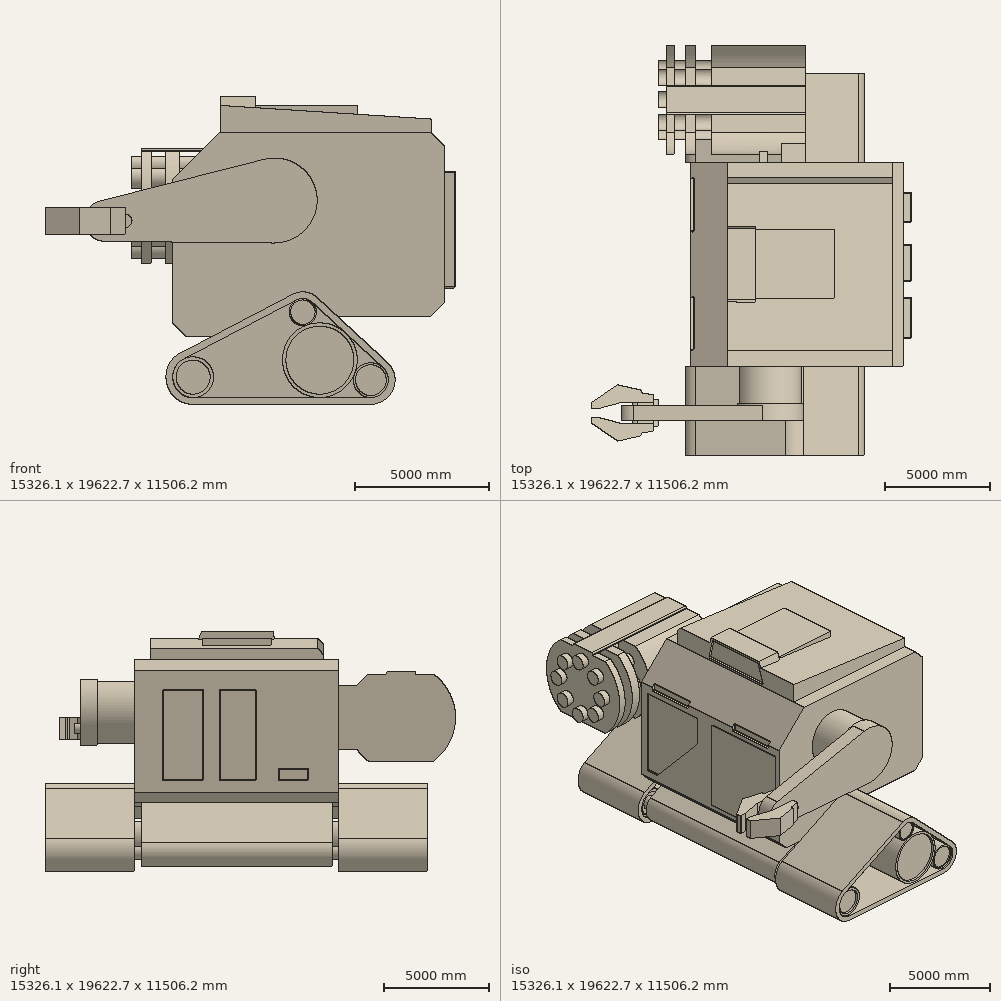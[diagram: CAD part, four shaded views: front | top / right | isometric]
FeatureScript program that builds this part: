
annotation { "Feature Type Name" : "Feature", "Feature Type Description" : "" }
export const myFeature = defineFeature(function(context is Context, id is Id, definition is map)
    precondition{}
    {
        {
            var Q0;
            Q0=qCreatedBy(makeId("Front.planeOp"),FACE);
            var sketch = newSketch(context, id + "F0", { "sketchPlane" : qUnion([Q0])});
            skCircle(sketch, "E0", {"center": v(762, 762) * mm, "radius": 762 * mm});
            skSolve(sketch);
        }
        {
            var Q0;
            Q0 = qSketchRegion(id + "F0", true);
            extrude(context, id + "F1", {"entities" : qUnion([Q0]), "oppositeDirection" : true, "depth" : 4064 * mm});
        }
        {
            var Q0;
            Q0=makeQuery(id+"F1.opExtrude","CAP_FACE",FACE,{"disambiguationData":[OSD([sQuery(id+"F0.wireOp",EDGE,"E0")])],"isStart":true});
            var sketch = newSketch(context, id + "F2", { "sketchPlane" : qUnion([Q0])});
            skCircle(sketch, "E1", {"center": v(762, 762) * mm, "radius": 635 * mm});
            skSolve(sketch);
        }
        {
            var Q0;
            Q0 = qSketchRegion(id + "F2", true);
            extrude(context, id + "F3", {"entities" : qUnion([Q0]), "operationType" : NewBodyOperationType.REMOVE, "oppositeDirection" : true, "depth" : 127 * mm});
        }
        {
            var Q0;
            Q0=makeQuery(id+"F1.opExtrude","CAP_FACE",FACE,{"disambiguationData":[OSD([sQuery(id+"F0.wireOp",EDGE,"E0")])],"isStart":false});
            var sketch = newSketch(context, id + "F4", { "sketchPlane" : qUnion([Q0])});
            skCircle(sketch, "E2", {"center": v(-762, 762) * mm, "radius": 635 * mm});
            skSolve(sketch);
        }
        {
            var Q0;
            Q0 = qSketchRegion(id + "F4", true);
            extrude(context, id + "F5", {"entities" : qUnion([Q0]), "operationType" : NewBodyOperationType.REMOVE, "oppositeDirection" : true, "depth" : 127 * mm});
        }
        {
            var Q0;
            Q0=qCreatedBy(makeId("Front.planeOp"),FACE);
            var sketch = newSketch(context, id + "F6", { "sketchPlane" : qUnion([Q0])});
            skLineSegment(sketch, "E3", {"start": v(0, 0) * mm, "end": v(8804.61, 0) * mm});
            skCircle(sketch, "E4", {"center": v(5497.48, 1397) * mm, "radius": 1397 * mm});
            skPoint(sketch, "E5", {"position": v(417.48, 431.63) * mm});
            skSolve(sketch);
        }
        {
            var Q0;
            Q0 = qSketchRegion(id + "F6", true);
            extrude(context, id + "F7", {"entities" : qUnion([Q0]), "oppositeDirection" : true, "depth" : 4064 * mm});
        }
        {
            var Q0;
            Q0=makeQuery(id+"F7.opExtrude","CAP_FACE",FACE,{"disambiguationData":[OSD([sQuery(id+"F6.wireOp",EDGE,"E4")])],"isStart":true});
            var sketch = newSketch(context, id + "F8", { "sketchPlane" : qUnion([Q0])});
            skCircle(sketch, "E6", {"center": v(5497.48, 1397) * mm, "radius": 1270 * mm});
            skSolve(sketch);
        }
        {
            var Q0;
            Q0 = qSketchRegion(id + "F8", true);
            extrude(context, id + "F9", {"entities" : qUnion([Q0]), "operationType" : NewBodyOperationType.REMOVE, "oppositeDirection" : true, "depth" : 127 * mm});
        }
        {
            var Q0;
            Q0=makeQuery(id+"F7.opExtrude","CAP_FACE",FACE,{"disambiguationData":[OSD([sQuery(id+"F6.wireOp",EDGE,"E4")])],"isStart":false});
            var sketch = newSketch(context, id + "F10", { "sketchPlane" : qUnion([Q0])});
            skCircle(sketch, "E7", {"center": v(-5497.48, 1397) * mm, "radius": 1270 * mm});
            skSolve(sketch);
        }
        {
            var Q0;
            Q0 = qSketchRegion(id + "F10", true);
            extrude(context, id + "F11", {"entities" : qUnion([Q0]), "operationType" : NewBodyOperationType.REMOVE, "oppositeDirection" : true, "depth" : 127 * mm});
        }
        {
            var Q0;
            Q0=qCreatedBy(makeId("Front.planeOp"),FACE);
            var sketch = newSketch(context, id + "F12", { "sketchPlane" : qUnion([Q0])});
            skCircle(sketch, "E8", {"center": v(4862.48, 3193.05) * mm, "radius": 508 * mm});
            skPoint(sketch, "E9", {"position": v(5497.48, 1397) * mm});
            skSolve(sketch);
        }
        {
            var Q0;
            Q0 = qSketchRegion(id + "F12", true);
            extrude(context, id + "F13", {"entities" : qUnion([Q0]), "operationType" : NewBodyOperationType.ADD, "oppositeDirection" : true, "depth" : 4064 * mm});
        }
        {
            var Q0;
            Q0=makeQuery(id+"F13.opExtrude","CAP_FACE",FACE,{"disambiguationData":[OSD([sQuery(id+"F12.wireOp",EDGE,"E8")])],"isStart":true});
            var sketch = newSketch(context, id + "F14", { "sketchPlane" : qUnion([Q0])});
            skCircle(sketch, "E10", {"center": v(4862.48, 3193.05) * mm, "radius": 457.2 * mm});
            skSolve(sketch);
        }
        {
            var Q0;
            Q0 = qSketchRegion(id + "F14", true);
            extrude(context, id + "F15", {"entities" : qUnion([Q0]), "operationType" : NewBodyOperationType.REMOVE, "oppositeDirection" : true, "depth" : 50.8 * mm});
        }
        {
            var Q0;
            Q0=makeQuery(id+"F13.opExtrude","CAP_FACE",FACE,{"disambiguationData":[OSD([sQuery(id+"F12.wireOp",EDGE,"E8")])],"isStart":false});
            var sketch = newSketch(context, id + "F16", { "sketchPlane" : qUnion([Q0])});
            skCircle(sketch, "E11", {"center": v(-4862.48, 3193.05) * mm, "radius": 457.2 * mm});
            skSolve(sketch);
        }
        {
            var Q0;
            Q0 = qSketchRegion(id + "F16", true);
            extrude(context, id + "F17", {"entities" : qUnion([Q0]), "operationType" : NewBodyOperationType.REMOVE, "oppositeDirection" : true, "depth" : 50.8 * mm});
        }
        {
            var Q0;
            Q0=qCreatedBy(makeId("Front.planeOp"),FACE);
            var sketch = newSketch(context, id + "F18", { "sketchPlane" : qUnion([Q0])});
            skLineSegment(sketch, "E12", {"start": v(330.5, 1396.25) * mm, "end": v(4640.98, 3650.5) * mm});
            skLineSegment(sketch, "E13", {"start": v(5195.5, 3576.98) * mm, "end": v(7846.69, 1129.63) * mm});
            skLineSegment(sketch, "E14", {"start": v(7405, 0) * mm, "end": v(673.56, 0) * mm});
            skArc(sketch, "E15", {"start": v(673.56, 0) * mm, "mid": v(17.04, 578.96) * mm, "end": v(330.5, 1396.25) * mm});
            skPoint(sketch, "E16.orphan", {"position": v(-2339.36, 0) * mm});
            skArc(sketch, "E17", {"start": v(4640.98, 3650.5) * mm, "mid": v(4929.27, 3696.89) * mm, "end": v(5195.5, 3576.98) * mm});
            skArc(sketch, "E18", {"start": v(7405, 0) * mm, "mid": v(8011.46, 414.04) * mm, "end": v(7846.69, 1129.63) * mm});
            skPoint(sketch, "E19.orphan", {"position": v(9070.4, 0) * mm});
            skLineSegment(sketch, "E20", {"start": v(212.8, 1621.33) * mm, "end": v(4520.5, 3874.12) * mm});
            skLineSegment(sketch, "E21", {"start": v(673.56, -254) * mm, "end": v(7405, -254) * mm});
            skLineSegment(sketch, "E22", {"start": v(5381.15, 3751.28) * mm, "end": v(8018.98, 1316.26) * mm});
            skArc(sketch, "E23", {"start": v(673.56, -254) * mm, "mid": v(-228.39, 518.66) * mm, "end": v(212.8, 1621.33) * mm});
            skArc(sketch, "E24", {"start": v(4520.5, 3874.12) * mm, "mid": v(4975.09, 3946.79) * mm, "end": v(5388.58, 3744.42) * mm});
            skArc(sketch, "E25", {"start": v(7405, -254) * mm, "mid": v(8248.02, 321.55) * mm, "end": v(8018.98, 1316.26) * mm});
            skSolve(sketch);
        }
        {
            var Q0;
            Q0 = qSketchRegion(id + "F18", true);
            extrude(context, id + "F19", {"entities" : qUnion([Q0]), "oppositeDirection" : true, "depth" : 4165.6 * mm, "hasSecondDirection" : true, "secondDirectionOppositeDirection" : false, "secondDirectionDepth" : 101.6 * mm});
        }
        {
            var Q0;
            Q0=qCreatedBy(makeId("Front.planeOp"),FACE);
            var sketch = newSketch(context, id + "F20", { "sketchPlane" : qUnion([Q0])});
            skCircle(sketch, "E26", {"center": v(7405, 651.16) * mm, "radius": 651.16 * mm});
            skSolve(sketch);
        }
        {
            var Q0;
            Q0 = qSketchRegion(id + "F20", true);
            extrude(context, id + "F21", {"entities" : qUnion([Q0]), "oppositeDirection" : true, "depth" : 4064 * mm});
        }
        {
            var Q0;
            Q0=makeQuery(id+"F21.opExtrude","CAP_FACE",FACE,{"disambiguationData":[OSD([sQuery(id+"F20.wireOp",EDGE,"E26")])],"isStart":false});
            var sketch = newSketch(context, id + "F22", { "sketchPlane" : qUnion([Q0])});
            skCircle(sketch, "E27", {"center": v(-7405, 651.16) * mm, "radius": 574.96 * mm});
            skSolve(sketch);
        }
        {
            var Q0;
            Q0 = qSketchRegion(id + "F22", true);
            extrude(context, id + "F23", {"entities" : qUnion([Q0]), "operationType" : NewBodyOperationType.REMOVE, "oppositeDirection" : true, "depth" : 76.2 * mm});
        }
        {
            var Q0;
            Q0=makeQuery(id+"F21.opExtrude","CAP_FACE",FACE,{"disambiguationData":[OSD([sQuery(id+"F20.wireOp",EDGE,"E26")])],"isStart":true});
            var sketch = newSketch(context, id + "F24", { "sketchPlane" : qUnion([Q0])});
            skCircle(sketch, "E28", {"center": v(7405, 651.16) * mm, "radius": 574.96 * mm});
            skSolve(sketch);
        }
        {
            var Q0;
            Q0 = qSketchRegion(id + "F24", true);
            extrude(context, id + "F25", {"entities" : qUnion([Q0]), "operationType" : NewBodyOperationType.REMOVE, "oppositeDirection" : true, "depth" : 76.2 * mm});
        }
        {
            var Q0;
            Q0=makeQuery(id+"F11.boolean.opBoolean","COPY",FACE,{"derivedFrom":makeQuery(id+"F11.opExtrude","CAP_FACE",FACE,{"disambiguationData":[OSD([sQuery(id+"F10.wireOp",EDGE,"E7")])],"isStart":false})});
            var sketch = newSketch(context, id + "F26", { "sketchPlane" : qUnion([Q0])});
            skCircle(sketch, "E29", {"center": v(-5497.48, 1397) * mm, "radius": 762 * mm});
            skCircle(sketch, "E30", {"center": v(-762, 762) * mm, "radius": 381 * mm});
            skCircle(sketch, "E31", {"center": v(-7405, 651.16) * mm, "radius": 320.96 * mm});
            skCircle(sketch, "E32", {"center": v(-4862.48, 3193.05) * mm, "radius": 330.2 * mm});
            skSolve(sketch);
        }
        {
            var Q0;
            Q0 = qSketchRegion(id + "F26", true);
            extrude(context, id + "F27", {"entities" : qUnion([Q0]), "depth" : 5080 * mm, "hasSecondDirection" : true, "secondDirectionOppositeDirection" : true, "secondDirectionDepth" : 254 * mm});
        }
        {
            var Q0;
            Q0=makeQuery(id+"F27.opExtrude","CAP_FACE",FACE,{"disambiguationData":[OSD([sQuery(id+"F26.wireOp",EDGE,"E32")])],"isStart":false});
            cPlane(context, id + "F28", {"entities" : qUnion([Q0]), "cplaneType" : CPlaneType.OFFSET, "offset" : 25.4 * mm, "width" : 152.4 * mm, "height" : 152.4 * mm});
        }
        {
            var Q0;
            Q0=makeQuery(id+"F1.opExtrude","SWEPT_BODY",BODY,{"disambiguationData":[OSD([sQuery(id+"F0.wireOp",EDGE,"E0")])]});
            var Q1;
            Q1=makeQuery(id+"F7.opExtrude","SWEPT_BODY",BODY,{"disambiguationData":[OSD([sQuery(id+"F6.wireOp",EDGE,"E4")])]});
            var Q2;
            Q2=makeQuery(id+"F13.opExtrude","SWEPT_BODY",BODY,{"disambiguationData":[OSD([sQuery(id+"F12.wireOp",EDGE,"E8")])]});
            var Q3;
            Q3=makeQuery(id+"F27.opExtrude","SWEPT_BODY",BODY,{"disambiguationData":[OSD([sQuery(id+"F26.wireOp",EDGE,"E32")])]});
            var Q4;
            Q4=makeQuery(id+"F27.opExtrude","SWEPT_BODY",BODY,{"disambiguationData":[OSD([sQuery(id+"F26.wireOp",EDGE,"E31")])]});
            var Q5;
            Q5=makeQuery(id+"F27.opExtrude","SWEPT_BODY",BODY,{"disambiguationData":[OSD([sQuery(id+"F26.wireOp",EDGE,"E30")])]});
            var Q6;
            Q6=makeQuery(id+"F27.opExtrude","SWEPT_BODY",BODY,{"disambiguationData":[OSD([sQuery(id+"F26.wireOp",EDGE,"E29")])]});
            var Q7;
            Q7=makeQuery(id+"F21.opExtrude","SWEPT_BODY",BODY,{"disambiguationData":[OSD([sQuery(id+"F20.wireOp",EDGE,"E26")])]});
            var Q8;
            Q8=makeQuery(id+"F19.opExtrude","SWEPT_BODY",BODY,{"disambiguationData":[OSD([sQuery(id+"F18.wireOp",EDGE,"E12"),sQuery(id+"F18.wireOp",EDGE,"E13"),sQuery(id+"F18.wireOp",EDGE,"E14"),sQuery(id+"F18.wireOp",EDGE,"E15"),sQuery(id+"F18.wireOp",EDGE,"E17"),sQuery(id+"F18.wireOp",EDGE,"E18"),sQuery(id+"F18.wireOp",EDGE,"E20"),sQuery(id+"F18.wireOp",EDGE,"E21"),sQuery(id+"F18.wireOp",EDGE,"E22"),sQuery(id+"F18.wireOp",EDGE,"E23"),sQuery(id+"F18.wireOp",EDGE,"E24"),sQuery(id+"F18.wireOp",EDGE,"E25")])]});
            var Q9;
            Q9=qCreatedBy(id+"F28.planeOp",FACE);
            mirror(context, id + "F29", {"entities" : qUnion([Q0, Q1, Q2, Q3, Q4, Q5, Q6, Q7, Q8]), "mirrorPlane" : qUnion([Q9])});
        }
        {
            var Q0;
            Q0=qCreatedBy(id+"F28.planeOp",FACE);
            var sketch = newSketch(context, id + "F30", { "sketchPlane" : qUnion([Q0])});
            skLineSegment(sketch, "E33", {"start": v(-4640.98, 3650.5) * mm, "end": v(-330.5, 1396.25) * mm});
            skLineSegment(sketch, "E34", {"start": v(-7846.69, 1129.63) * mm, "end": v(-5195.5, 3576.98) * mm});
            skLineSegment(sketch, "E35", {"start": v(-673.56, 0) * mm, "end": v(-7405, 0) * mm});
            skPoint(sketch, "E36", {"position": v(-4862.48, 3193.05) * mm});
            skArc(sketch, "E37", {"start": v(-5195.5, 3576.98) * mm, "mid": v(-4929.27, 3696.89) * mm, "end": v(-4640.98, 3650.5) * mm});
            skPoint(sketch, "E38", {"position": v(-762, 762) * mm});
            skArc(sketch, "E39", {"start": v(-330.5, 1396.25) * mm, "mid": v(-17.04, 578.96) * mm, "end": v(-673.56, 0) * mm});
            skPoint(sketch, "E40", {"position": v(-7405, 651.16) * mm});
            skArc(sketch, "E41", {"start": v(-7405, 0) * mm, "mid": v(-8011.46, 414.04) * mm, "end": v(-7846.69, 1129.63) * mm});
            skSolve(sketch);
        }
        {
            var Q0;
            Q0 = qSketchRegion(id + "F30", true);
            extrude(context, id + "F31", {"entities" : qUnion([Q0]), "depth" : 4572 * mm, "hasSecondDirection" : true, "secondDirectionOppositeDirection" : true, "secondDirectionDepth" : 4572 * mm});
        }
        {
            var Q0;
            Q0=qCreatedBy(id+"F28.planeOp",FACE);
            var sketch = newSketch(context, id + "F32", { "sketchPlane" : qUnion([Q0])});
            skLineSegment(sketch, "E42", {"start": v(-5768.54, 3048) * mm, "end": v(-10160, 3048) * mm});
            skLineSegment(sketch, "E43", {"start": v(-10160, 3048) * mm, "end": v(-10160, 9906) * mm});
            skLineSegment(sketch, "E44", {"start": v(-10160, 9906) * mm, "end": v(0, 9906) * mm});
            skLineSegment(sketch, "E45", {"start": v(0, 9906) * mm, "end": v(0, 2286) * mm});
            skLineSegment(sketch, "E46", {"start": v(0, 2286) * mm, "end": v(-2031.85, 2286) * mm});
            skPoint(sketch, "E47", {"position": v(-4862.48, 3193.05) * mm});
            skPoint(sketch, "E48.orphan", {"position": v(-4984.96, 4117.02) * mm});
            skArc(sketch, "E49", {"start": v(-5226.07, 3547.92) * mm, "mid": v(-4934.21, 3696.03) * mm, "end": v(-4612.58, 3635.42) * mm});
            skLineSegment(sketch, "E50", {"start": v(-5768.54, 3048) * mm, "end": v(-5226.07, 3547.92) * mm});
            skLineSegment(sketch, "E51", {"start": v(-4612.58, 3635.42) * mm, "end": v(-2031.85, 2286) * mm});
            skSolve(sketch);
        }
        {
            var Q0;
            Q0 = qSketchRegion(id + "F32", true);
            extrude(context, id + "F33", {"entities" : qUnion([Q0]), "depth" : 4876.8 * mm, "hasSecondDirection" : true, "secondDirectionOppositeDirection" : true, "secondDirectionDepth" : 4876.8 * mm});
        }
        {
            var Q0;
            Q0=makeQuery(id+"F33.opExtrude","SWEPT_EDGE",EDGE,{"disambiguationData":[OSD([sQuery(id+"F32.wireOp",EDGE,"E44"),sQuery(id+"F32.wireOp",EDGE,"E45")])]});
            chamfer(context, id + "F34", {"entities" : qUnion([Q0]), "width" : 1778 * mm, "tangentPropagation" : true});
        }
        {
            var Q0;
            Q0=makeQuery(id+"F33.opExtrude","SWEPT_EDGE",EDGE,{"disambiguationData":[OSD([sQuery(id+"F32.wireOp",EDGE,"E43"),sQuery(id+"F32.wireOp",EDGE,"E44")])]});
            var Q1;
            Q1=makeQuery(id+"F33.opExtrude","SWEPT_EDGE",EDGE,{"disambiguationData":[OSD([sQuery(id+"F32.wireOp",EDGE,"E42"),sQuery(id+"F32.wireOp",EDGE,"E43")])]});
            chamfer(context, id + "F35", {"entities" : qUnion([Q0, Q1]), "width" : 508 * mm, "tangentPropagation" : true});
        }
        {
            var Q0;
            Q0=makeQuery(id+"F33.opExtrude","SWEPT_EDGE",EDGE,{"disambiguationData":[OSD([sQuery(id+"F32.wireOp",EDGE,"E45"),sQuery(id+"F32.wireOp",EDGE,"E46")])]});
            chamfer(context, id + "F36", {"entities" : qUnion([Q0]), "width" : 508 * mm, "tangentPropagation" : true});
        }
        {
            var Q0;
            Q0=makeQuery(id+"F33.opExtrude","SWEPT_FACE",FACE,{"disambiguationData":[OSD([sQuery(id+"F32.wireOp",EDGE,"E43")])]});
            var sketch = newSketch(context, id + "F37", { "sketchPlane" : qUnion([Q0])});
            skLineSegment(sketch, "E52.bottom", {"start": v(5510.46, 8459.44) * mm, "end": v(7459.12, 8459.44) * mm});
            skLineSegment(sketch, "E52.top", {"start": v(5510.46, 4095.25) * mm, "end": v(7459.12, 4095.25) * mm});
            skLineSegment(sketch, "E52.left", {"start": v(5510.46, 8459.44) * mm, "end": v(5510.46, 4095.25) * mm});
            skLineSegment(sketch, "E52.right", {"start": v(7459.12, 8459.44) * mm, "end": v(7459.12, 4095.25) * mm});
            skLineSegment(sketch, "E53.bottom", {"start": v(8230.46, 8459.44) * mm, "end": v(9976.13, 8459.44) * mm});
            skLineSegment(sketch, "E53.top", {"start": v(8230.46, 4095.25) * mm, "end": v(9976.13, 4095.25) * mm});
            skLineSegment(sketch, "E53.left", {"start": v(8230.46, 8459.44) * mm, "end": v(8230.46, 4095.25) * mm});
            skLineSegment(sketch, "E53.right", {"start": v(9976.13, 8459.44) * mm, "end": v(9976.13, 4095.25) * mm});
            skLineSegment(sketch, "E54.bottom", {"start": v(11051.95, 4095.25) * mm, "end": v(12472.85, 4095.25) * mm});
            skLineSegment(sketch, "E54.top", {"start": v(11051.95, 4683.91) * mm, "end": v(12472.85, 4683.91) * mm});
            skLineSegment(sketch, "E54.left", {"start": v(11051.95, 4095.25) * mm, "end": v(11051.95, 4683.91) * mm});
            skLineSegment(sketch, "E54.right", {"start": v(12472.85, 4095.25) * mm, "end": v(12472.85, 4683.91) * mm});
            skSolve(sketch);
        }
        {
            var Q0;
            Q0 = qSketchRegion(id + "F37", true);
            extrude(context, id + "F38", {"entities" : qUnion([Q0]), "operationType" : NewBodyOperationType.ADD, "depth" : 406.4 * mm});
        }
        {
            var Q0;
            Q0=makeQuery(id+"F38.opExtrude","CAP_FACE",FACE,{"disambiguationData":[OSD([sQuery(id+"F37.wireOp",EDGE,"E52.bottom"),sQuery(id+"F37.wireOp",EDGE,"E52.top"),sQuery(id+"F37.wireOp",EDGE,"E52.left"),sQuery(id+"F37.wireOp",EDGE,"E52.right")])],"isStart":false});
            var Q1;
            Q1=makeQuery(id+"F38.opExtrude","CAP_FACE",FACE,{"disambiguationData":[OSD([sQuery(id+"F37.wireOp",EDGE,"E53.bottom"),sQuery(id+"F37.wireOp",EDGE,"E53.top"),sQuery(id+"F37.wireOp",EDGE,"E53.left"),sQuery(id+"F37.wireOp",EDGE,"E53.right")])],"isStart":false});
            var Q2;
            Q2=makeQuery(id+"F38.opExtrude","CAP_FACE",FACE,{"disambiguationData":[OSD([sQuery(id+"F37.wireOp",EDGE,"E54.bottom"),sQuery(id+"F37.wireOp",EDGE,"E54.top"),sQuery(id+"F37.wireOp",EDGE,"E54.left"),sQuery(id+"F37.wireOp",EDGE,"E54.right")])],"isStart":false});
            var Q3;
            Q3=makeQuery(id+"F38.opExtrude","SWEPT_EDGE",EDGE,{"disambiguationData":[OSD([sQuery(id+"F37.wireOp",EDGE,"E52.bottom"),sQuery(id+"F37.wireOp",EDGE,"E52.left")])]});
            var Q4;
            Q4=makeQuery(id+"F38.opExtrude","SWEPT_EDGE",EDGE,{"disambiguationData":[OSD([sQuery(id+"F37.wireOp",EDGE,"E52.bottom"),sQuery(id+"F37.wireOp",EDGE,"E52.right")])]});
            var Q5;
            Q5=makeQuery(id+"F38.opExtrude","SWEPT_EDGE",EDGE,{"disambiguationData":[OSD([sQuery(id+"F37.wireOp",EDGE,"E52.top"),sQuery(id+"F37.wireOp",EDGE,"E52.left")])]});
            var Q6;
            Q6=makeQuery(id+"F38.opExtrude","SWEPT_EDGE",EDGE,{"disambiguationData":[OSD([sQuery(id+"F37.wireOp",EDGE,"E52.top"),sQuery(id+"F37.wireOp",EDGE,"E52.right")])]});
            var Q7;
            Q7=makeQuery(id+"F38.opExtrude","SWEPT_EDGE",EDGE,{"disambiguationData":[OSD([sQuery(id+"F37.wireOp",EDGE,"E53.top"),sQuery(id+"F37.wireOp",EDGE,"E53.left")])]});
            var Q8;
            Q8=makeQuery(id+"F38.opExtrude","SWEPT_EDGE",EDGE,{"disambiguationData":[OSD([sQuery(id+"F37.wireOp",EDGE,"E53.top"),sQuery(id+"F37.wireOp",EDGE,"E53.right")])]});
            var Q9;
            Q9=makeQuery(id+"F38.opExtrude","SWEPT_EDGE",EDGE,{"disambiguationData":[OSD([sQuery(id+"F37.wireOp",EDGE,"E53.bottom"),sQuery(id+"F37.wireOp",EDGE,"E53.right")])]});
            var Q10;
            Q10=makeQuery(id+"F38.opExtrude","SWEPT_EDGE",EDGE,{"disambiguationData":[OSD([sQuery(id+"F37.wireOp",EDGE,"E53.bottom"),sQuery(id+"F37.wireOp",EDGE,"E53.left")])]});
            var Q11;
            Q11=makeQuery(id+"F38.opExtrude","SWEPT_EDGE",EDGE,{"disambiguationData":[OSD([sQuery(id+"F37.wireOp",EDGE,"E54.top"),sQuery(id+"F37.wireOp",EDGE,"E54.left")])]});
            var Q12;
            Q12=makeQuery(id+"F38.opExtrude","SWEPT_EDGE",EDGE,{"disambiguationData":[OSD([sQuery(id+"F37.wireOp",EDGE,"E54.bottom"),sQuery(id+"F37.wireOp",EDGE,"E54.left")])]});
            var Q13;
            Q13=makeQuery(id+"F38.opExtrude","SWEPT_EDGE",EDGE,{"disambiguationData":[OSD([sQuery(id+"F37.wireOp",EDGE,"E54.bottom"),sQuery(id+"F37.wireOp",EDGE,"E54.right")])]});
            var Q14;
            Q14=makeQuery(id+"F38.opExtrude","SWEPT_EDGE",EDGE,{"disambiguationData":[OSD([sQuery(id+"F37.wireOp",EDGE,"E54.top"),sQuery(id+"F37.wireOp",EDGE,"E54.right")])]});
            fillet(context, id + "F39", {"entities" : qUnion([Q0, Q1, Q2, Q3, Q4, Q5, Q6, Q7, Q8, Q9, Q10, Q11, Q12, Q13, Q14]), "radius" : 50.8 * mm, "tangentPropagation" : true, "allowEdgeOverflow" : false});
        }
        {
            var Q0;
            Q0=makeQuery(id+"F33.opExtrude","SWEPT_FACE",FACE,{"disambiguationData":[OSD([sQuery(id+"F32.wireOp",EDGE,"E45")])]});
            var sketch = newSketch(context, id + "F40", { "sketchPlane" : qUnion([Q0])});
            skLineSegment(sketch, "E55.bottom", {"start": v(-13157.2, 8331.2) * mm, "end": v(-10617.2, 8331.2) * mm});
            skLineSegment(sketch, "E55.top", {"start": v(-13157.2, 7924.8) * mm, "end": v(-10617.2, 7924.8) * mm});
            skLineSegment(sketch, "E55.left", {"start": v(-13157.2, 8331.2) * mm, "end": v(-13157.2, 7924.8) * mm});
            skLineSegment(sketch, "E55.right", {"start": v(-10617.2, 8331.2) * mm, "end": v(-10617.2, 7924.8) * mm});
            skLineSegment(sketch, "E56.bottom", {"start": v(-7467.6, 8331.2) * mm, "end": v(-4927.6, 8331.2) * mm});
            skLineSegment(sketch, "E56.top", {"start": v(-7467.6, 7924.8) * mm, "end": v(-4927.6, 7924.8) * mm});
            skLineSegment(sketch, "E56.left", {"start": v(-7467.6, 8331.2) * mm, "end": v(-7467.6, 7924.8) * mm});
            skLineSegment(sketch, "E56.right", {"start": v(-4927.6, 8331.2) * mm, "end": v(-4927.6, 7924.8) * mm});
            skSolve(sketch);
        }
        {
            var Q0;
            Q0 = qSketchRegion(id + "F40", true);
            extrude(context, id + "F41", {"entities" : qUnion([Q0]), "operationType" : NewBodyOperationType.REMOVE, "oppositeDirection" : true, "depth" : 144.78 * mm});
        }
        {
            var Q0;
            Q0=makeQuery(id+"F41.boolean.opBoolean","COPY",FACE,{"derivedFrom":makeQuery(id+"F41.opExtrude","CAP_FACE",FACE,{"disambiguationData":[OSD([sQuery(id+"F40.wireOp",EDGE,"E55.bottom"),sQuery(id+"F40.wireOp",EDGE,"E55.top"),sQuery(id+"F40.wireOp",EDGE,"E55.left"),sQuery(id+"F40.wireOp",EDGE,"E55.right")])],"isStart":false})});
            var Q1;
            Q1=makeQuery(id+"F41.boolean.opBoolean","COPY",FACE,{"derivedFrom":makeQuery(id+"F41.opExtrude","CAP_FACE",FACE,{"disambiguationData":[OSD([sQuery(id+"F40.wireOp",EDGE,"E56.bottom"),sQuery(id+"F40.wireOp",EDGE,"E56.top"),sQuery(id+"F40.wireOp",EDGE,"E56.left"),sQuery(id+"F40.wireOp",EDGE,"E56.right")])],"isStart":false})});
            var Q2;
            Q2=makeQuery(id+"F41.boolean.opBoolean","COPY",EDGE,{"derivedFrom":makeQuery(id+"F41.opExtrude","SWEPT_EDGE",EDGE,{"disambiguationData":[OSD([sQuery(id+"F40.wireOp",EDGE,"E55.top"),sQuery(id+"F40.wireOp",EDGE,"E55.left")])]})});
            var Q3;
            Q3=makeQuery(id+"F41.boolean.opBoolean","COPY",EDGE,{"derivedFrom":makeQuery(id+"F41.opExtrude","SWEPT_EDGE",EDGE,{"disambiguationData":[OSD([sQuery(id+"F40.wireOp",EDGE,"E55.top"),sQuery(id+"F40.wireOp",EDGE,"E55.right")])]})});
            var Q4;
            Q4=makeQuery(id+"F41.boolean.opBoolean","COPY",EDGE,{"derivedFrom":makeQuery(id+"F41.opExtrude","SWEPT_EDGE",EDGE,{"disambiguationData":[OSD([sQuery(id+"F40.wireOp",EDGE,"E56.top"),sQuery(id+"F40.wireOp",EDGE,"E56.left")])]})});
            var Q5;
            Q5=makeQuery(id+"F41.boolean.opBoolean","COPY",EDGE,{"derivedFrom":makeQuery(id+"F41.opExtrude","SWEPT_EDGE",EDGE,{"disambiguationData":[OSD([sQuery(id+"F40.wireOp",EDGE,"E56.top"),sQuery(id+"F40.wireOp",EDGE,"E56.right")])]})});
            fillet(context, id + "F42", {"entities" : qUnion([Q0, Q1, Q2, Q3, Q4, Q5]), "radius" : 25.4 * mm, "tangentPropagation" : true, "allowEdgeOverflow" : false});
        }
        {
            var Q0;
            Q0=makeQuery(id+"F33.opExtrude","SWEPT_FACE",FACE,{"disambiguationData":[OSD([sQuery(id+"F32.wireOp",EDGE,"E45")])]});
            var sketch = newSketch(context, id + "F43", { "sketchPlane" : qUnion([Q0])});
            skLineSegment(sketch, "E57", {"start": v(-13538.2, 3175) * mm, "end": v(-13538.2, 7620) * mm});
            skLineSegment(sketch, "E58", {"start": v(-13538.2, 7620) * mm, "end": v(-9982.2, 7620) * mm});
            skLineSegment(sketch, "E59", {"start": v(-9982.2, 7620) * mm, "end": v(-9982.2, 6096) * mm});
            skLineSegment(sketch, "E60", {"start": v(-9982.2, 6096) * mm, "end": v(-12776.2, 3175) * mm});
            skLineSegment(sketch, "E61", {"start": v(-12776.2, 3175) * mm, "end": v(-13538.2, 3175) * mm});
            skSolve(sketch);
        }
        {
            var Q0;
            Q0 = qSketchRegion(id + "F43", true);
            extrude(context, id + "F44", {"entities" : qUnion([Q0]), "operationType" : NewBodyOperationType.REMOVE, "oppositeDirection" : true, "depth" : 101.6 * mm});
        }
        {
            var Q0;
            Q0=makeQuery(id+"F44.boolean.opBoolean","COPY",EDGE,{"derivedFrom":makeQuery(id+"F44.opExtrude","SWEPT_EDGE",EDGE,{"disambiguationData":[OSD([sQuery(id+"F43.wireOp",EDGE,"E57"),sQuery(id+"F43.wireOp",EDGE,"E58")])]})});
            var Q1;
            Q1=makeQuery(id+"F44.boolean.opBoolean","COPY",EDGE,{"derivedFrom":makeQuery(id+"F44.opExtrude","SWEPT_EDGE",EDGE,{"disambiguationData":[OSD([sQuery(id+"F43.wireOp",EDGE,"E58"),sQuery(id+"F43.wireOp",EDGE,"E59")])]})});
            var Q2;
            Q2=makeQuery(id+"F44.boolean.opBoolean","COPY",EDGE,{"derivedFrom":makeQuery(id+"F44.opExtrude","SWEPT_EDGE",EDGE,{"disambiguationData":[OSD([sQuery(id+"F43.wireOp",EDGE,"E59"),sQuery(id+"F43.wireOp",EDGE,"E60")])]})});
            var Q3;
            Q3=makeQuery(id+"F44.boolean.opBoolean","COPY",EDGE,{"derivedFrom":makeQuery(id+"F44.opExtrude","SWEPT_EDGE",EDGE,{"disambiguationData":[OSD([sQuery(id+"F43.wireOp",EDGE,"E60"),sQuery(id+"F43.wireOp",EDGE,"E61")])]})});
            var Q4;
            Q4=makeQuery(id+"F44.boolean.opBoolean","COPY",EDGE,{"derivedFrom":makeQuery(id+"F44.opExtrude","SWEPT_EDGE",EDGE,{"disambiguationData":[OSD([sQuery(id+"F43.wireOp",EDGE,"E57"),sQuery(id+"F43.wireOp",EDGE,"E61")])]})});
            fillet(context, id + "F45", {"entities" : qUnion([Q0, Q1, Q2, Q3, Q4]), "radius" : 50.8 * mm, "tangentPropagation" : true, "allowEdgeOverflow" : false});
        }
        {
            var Q0;
            Q0=makeQuery(id+"F33.opExtrude","SWEPT_FACE",FACE,{"disambiguationData":[OSD([sQuery(id+"F32.wireOp",EDGE,"E45")])]});
            var sketch = newSketch(context, id + "F46", { "sketchPlane" : qUnion([Q0])});
            skLineSegment(sketch, "E62.bottom", {"start": v(-4419.6, 3048) * mm, "end": v(-8966.2, 3048) * mm});
            skLineSegment(sketch, "E62.top", {"start": v(-4419.6, 7670.8) * mm, "end": v(-8966.2, 7670.8) * mm});
            skLineSegment(sketch, "E62.left", {"start": v(-4419.6, 3048) * mm, "end": v(-4419.6, 7670.8) * mm});
            skLineSegment(sketch, "E62.right", {"start": v(-8966.2, 3048) * mm, "end": v(-8966.2, 7670.8) * mm});
            skSolve(sketch);
        }
        {
            var Q0;
            Q0 = qSketchRegion(id + "F46", true);
            extrude(context, id + "F47", {"entities" : qUnion([Q0]), "operationType" : NewBodyOperationType.ADD, "depth" : 25.4 * mm});
        }
        {
            var Q0;
            Q0=makeQuery(id+"F47.opExtrude","SWEPT_EDGE",EDGE,{"disambiguationData":[OSD([sQuery(id+"F46.wireOp",EDGE,"E62.top"),sQuery(id+"F46.wireOp",EDGE,"E62.right")])]});
            var Q1;
            Q1=makeQuery(id+"F47.opExtrude","SWEPT_EDGE",EDGE,{"disambiguationData":[OSD([sQuery(id+"F46.wireOp",EDGE,"E62.top"),sQuery(id+"F46.wireOp",EDGE,"E62.left")])]});
            var Q2;
            Q2=makeQuery(id+"F47.opExtrude","SWEPT_EDGE",EDGE,{"disambiguationData":[OSD([sQuery(id+"F46.wireOp",EDGE,"E62.bottom"),sQuery(id+"F46.wireOp",EDGE,"E62.left")])]});
            var Q3;
            Q3=makeQuery(id+"F47.opExtrude","SWEPT_EDGE",EDGE,{"disambiguationData":[OSD([sQuery(id+"F46.wireOp",EDGE,"E62.bottom"),sQuery(id+"F46.wireOp",EDGE,"E62.right")])]});
            fillet(context, id + "F48", {"entities" : qUnion([Q0, Q1, Q2, Q3]), "radius" : 50.8 * mm, "tangentPropagation" : true, "allowEdgeOverflow" : false});
        }
        {
            var Q0;
            Q0=makeQuery(id+"F33.opExtrude","CAP_FACE",FACE,{"disambiguationData":[OSD([sQuery(id+"F32.wireOp",EDGE,"E42"),sQuery(id+"F32.wireOp",EDGE,"E43"),sQuery(id+"F32.wireOp",EDGE,"E44"),sQuery(id+"F32.wireOp",EDGE,"E45"),sQuery(id+"F32.wireOp",EDGE,"E46"),sQuery(id+"F32.wireOp",EDGE,"E49"),sQuery(id+"F32.wireOp",EDGE,"E50"),sQuery(id+"F32.wireOp",EDGE,"E51")])],"isStart":true});
            var sketch = newSketch(context, id + "F49", { "sketchPlane" : qUnion([Q0])});
            skCircle(sketch, "E63", {"center": v(3810, 7366) * mm, "radius": 1467.94 * mm});
            skSolve(sketch);
        }
        {
            var Q0;
            Q0 = qSketchRegion(id + "F49", true);
            extrude(context, id + "F50", {"entities" : qUnion([Q0]), "operationType" : NewBodyOperationType.ADD, "depth" : 2540 * mm});
        }
        {
            var Q0;
            Q0=makeQuery(id+"F50.opExtrude","CAP_FACE",FACE,{"disambiguationData":[OSD([sQuery(id+"F49.wireOp",EDGE,"E63")])],"isStart":false});
            var sketch = newSketch(context, id + "F51", { "sketchPlane" : qUnion([Q0])});
            skCircle(sketch, "E64", {"center": v(3810, 7366) * mm, "radius": 1587.5 * mm});
            skSolve(sketch);
        }
        {
            var Q0;
            Q0 = qSketchRegion(id + "F51", true);
            extrude(context, id + "F52", {"entities" : qUnion([Q0]), "operationType" : NewBodyOperationType.ADD, "depth" : 76.2 * mm, "hasSecondDirection" : true, "secondDirectionOppositeDirection" : true, "secondDirectionDepth" : 762 * mm});
        }
        {
            var Q0;
            Q0=makeQuery(id+"F52.opExtrude","CAP_FACE",FACE,{"disambiguationData":[OSD([sQuery(id+"F51.wireOp",EDGE,"E64")])],"isStart":false});
            var sketch = newSketch(context, id + "F53", { "sketchPlane" : qUnion([Q0])});
            skArc(sketch, "E65", {"start": v(3794.12, 5778.58) * mm, "mid": v(5386.2, 7555.14) * mm, "end": v(3419, 8904.6) * mm});
            skArc(sketch, "E66", {"start": v(-2727.68, 7342.52) * mm, "mid": v(-3296.57, 6513.21) * mm, "end": v(-2547.62, 5842.04) * mm});
            skLineSegment(sketch, "E67", {"start": v(-2727.68, 7342.52) * mm, "end": v(3419, 8904.6) * mm});
            skLineSegment(sketch, "E68", {"start": v(-2547.62, 5842.04) * mm, "end": v(3794.12, 5778.58) * mm});
            skSolve(sketch);
        }
        {
            var Q0;
            Q0 = qSketchRegion(id + "F53", true);
            extrude(context, id + "F54", {"entities" : qUnion([Q0]), "operationType" : NewBodyOperationType.ADD, "oppositeDirection" : true, "depth" : 762 * mm});
        }
        {
            var Q0;
            Q0=makeQuery(id+"F54.boolean.opBoolean","MERGE",FACE,{"derivedFrom":[makeQuery(id+"F52.opExtrude","CAP_FACE",FACE,{"disambiguationData":[OSD([sQuery(id+"F51.wireOp",EDGE,"E64")])],"isStart":false}),makeQuery(id+"F54.opExtrude","CAP_FACE",FACE,{"disambiguationData":[OSD([sQuery(id+"F53.wireOp",EDGE,"E65"),sQuery(id+"F53.wireOp",EDGE,"E66"),sQuery(id+"F53.wireOp",EDGE,"E67"),sQuery(id+"F53.wireOp",EDGE,"E68")])],"isStart":true})]});
            var sketch = newSketch(context, id + "F55", { "sketchPlane" : qUnion([Q0])});
            skLineSegment(sketch, "E69.bottom", {"start": v(-2540, 6858) * mm, "end": v(-1778, 6858) * mm});
            skLineSegment(sketch, "E69.top", {"start": v(-2540, 6350) * mm, "end": v(-1778, 6350) * mm});
            skArc(sketch, "E70", {"start": v(-1778, 6350) * mm, "mid": v(-1524, 6604) * mm, "end": v(-1778, 6858) * mm});
            skArc(sketch, "E71", {"start": v(-2540, 6858) * mm, "mid": v(-2794, 6604) * mm, "end": v(-2540, 6350) * mm});
            skSolve(sketch);
        }
        {
            var Q0;
            Q0 = qSketchRegion(id + "F55", true);
            extrude(context, id + "F56", {"entities" : qUnion([Q0]), "operationType" : NewBodyOperationType.ADD, "depth" : 254 * mm, "hasSecondDirection" : true, "secondDirectionOppositeDirection" : true, "secondDirectionDepth" : 1016 * mm});
        }
        {
            var Q0;
            {var subQ2=sQuery(id+"F55.wireOp",EDGE,"E69.bottom");Q0=makeQuery(id+"F56.boolean.opBoolean","SPLIT",FACE,{"disambiguationData":[TD([makeQuery(id+"F52.opExtrude","CAP_FACE",FACE,{"disambiguationData":[OSD([sQuery(id+"F51.wireOp",EDGE,"E64")])],"isStart":false})])],"derivedFrom":makeQuery(id+"F56.opExtrude","SWEPT_FACE",FACE,{"disambiguationData":[OSD([subQ2])]})});}
            var sketch = newSketch(context, id + "F57", { "sketchPlane" : qUnion([Q0])});
            skLineSegment(sketch, "E72", {"start": v(-1778, 2438.4) * mm, "end": v(-3291.95, 2438.4) * mm});
            skLineSegment(sketch, "E73", {"start": v(-3291.95, 2438.4) * mm, "end": v(-4429.48, 2133.6) * mm});
            skLineSegment(sketch, "E74", {"start": v(-4429.48, 2133.6) * mm, "end": v(-4759.68, 2133.6) * mm});
            skLineSegment(sketch, "E75", {"start": v(-4759.68, 2133.6) * mm, "end": v(-4759.68, 2413) * mm});
            skLineSegment(sketch, "E76", {"start": v(-4759.68, 2413) * mm, "end": v(-3489.68, 3276.6) * mm});
            skLineSegment(sketch, "E77", {"start": v(-3489.68, 3276.6) * mm, "end": v(-2346.68, 3019.53) * mm});
            skLineSegment(sketch, "E78", {"start": v(-2346.68, 3019.53) * mm, "end": v(-2336.8, 2892.53) * mm});
            skLineSegment(sketch, "E79", {"start": v(-2336.8, 2892.53) * mm, "end": v(-1778, 2794) * mm});
            skLineSegment(sketch, "E80", {"start": v(-1778, 2794) * mm, "end": v(-1778, 2438.4) * mm});
            skLineSegment(sketch, "E81", {"start": v(-4759.68, 1930.4) * mm, "end": v(-1014.61, 1930.4) * mm});
            skLineSegment(sketch, "E82.MirrorCS", {"start": v(-3291.95, 1422.4) * mm, "end": v(-4429.48, 1727.2) * mm});
            skLineSegment(sketch, "E83.MirrorCS", {"start": v(-4429.48, 1727.2) * mm, "end": v(-4759.68, 1727.2) * mm});
            skLineSegment(sketch, "E84.MirrorCS", {"start": v(-4759.68, 1727.2) * mm, "end": v(-4759.68, 1447.8) * mm});
            skLineSegment(sketch, "E85.MirrorCS", {"start": v(-4759.68, 1447.8) * mm, "end": v(-3489.68, 584.2) * mm});
            skLineSegment(sketch, "E86.MirrorCS", {"start": v(-3489.68, 584.2) * mm, "end": v(-2346.68, 841.27) * mm});
            skLineSegment(sketch, "E87.MirrorCS", {"start": v(-2346.68, 841.27) * mm, "end": v(-2336.8, 968.27) * mm});
            skLineSegment(sketch, "E88.MirrorCS", {"start": v(-2336.8, 968.27) * mm, "end": v(-1778, 1066.8) * mm});
            skLineSegment(sketch, "E89.MirrorCS", {"start": v(-1778, 1066.8) * mm, "end": v(-1778, 1422.4) * mm});
            skLineSegment(sketch, "E90.MirrorCS", {"start": v(-1778, 1422.4) * mm, "end": v(-3291.95, 1422.4) * mm});
            skSolve(sketch);
        }
        {
            var Q0;
            Q0 = qSketchRegion(id + "F57", true);
            extrude(context, id + "F58", {"entities" : qUnion([Q0]), "operationType" : NewBodyOperationType.ADD, "oppositeDirection" : true, "depth" : 762 * mm, "hasSecondDirection" : true, "secondDirectionOppositeDirection" : false, "secondDirectionDepth" : 254 * mm});
        }
        {
            var Q0;
            Q0=makeQuery(id+"F58.opExtrude","SWEPT_EDGE",EDGE,{"disambiguationData":[OSD([sQuery(id+"F57.wireOp",EDGE,"E74"),sQuery(id+"F57.wireOp",EDGE,"E75")])]});
            var Q1;
            Q1=makeQuery(id+"F58.opExtrude","SWEPT_EDGE",EDGE,{"disambiguationData":[OSD([sQuery(id+"F57.wireOp",EDGE,"E83.MirrorCS"),sQuery(id+"F57.wireOp",EDGE,"E84.MirrorCS")])]});
            var Q2;
            Q2=makeQuery(id+"F58.opExtrude","SWEPT_EDGE",EDGE,{"disambiguationData":[OSD([sQuery(id+"F57.wireOp",EDGE,"E84.MirrorCS"),sQuery(id+"F57.wireOp",EDGE,"E85.MirrorCS")])]});
            var Q3;
            Q3=makeQuery(id+"F58.opExtrude","SWEPT_EDGE",EDGE,{"disambiguationData":[OSD([sQuery(id+"F57.wireOp",EDGE,"E75"),sQuery(id+"F57.wireOp",EDGE,"E76")])]});
            var Q4;
            Q4=makeQuery(id+"F58.opExtrude","SWEPT_EDGE",EDGE,{"disambiguationData":[OSD([sQuery(id+"F57.wireOp",EDGE,"E73"),sQuery(id+"F57.wireOp",EDGE,"E74")])]});
            var Q5;
            Q5=makeQuery(id+"F58.opExtrude","SWEPT_EDGE",EDGE,{"disambiguationData":[OSD([sQuery(id+"F57.wireOp",EDGE,"E82.MirrorCS"),sQuery(id+"F57.wireOp",EDGE,"E83.MirrorCS")])]});
            var Q6;
            Q6=makeQuery(id+"F58.opExtrude","SWEPT_EDGE",EDGE,{"disambiguationData":[OSD([sQuery(id+"F57.wireOp",EDGE,"E85.MirrorCS"),sQuery(id+"F57.wireOp",EDGE,"E86.MirrorCS")])]});
            var Q7;
            Q7=makeQuery(id+"F58.opExtrude","SWEPT_EDGE",EDGE,{"disambiguationData":[OSD([sQuery(id+"F57.wireOp",EDGE,"E76"),sQuery(id+"F57.wireOp",EDGE,"E77")])]});
            fillet(context, id + "F59", {"entities" : qUnion([Q0, Q1, Q2, Q3, Q4, Q5, Q6, Q7]), "radius" : 25.4 * mm, "tangentPropagation" : true, "allowEdgeOverflow" : false});
        }
        {
            var Q0;
            Q0=makeQuery(id+"F33.opExtrude","CAP_FACE",FACE,{"disambiguationData":[OSD([sQuery(id+"F32.wireOp",EDGE,"E42"),sQuery(id+"F32.wireOp",EDGE,"E43"),sQuery(id+"F32.wireOp",EDGE,"E44"),sQuery(id+"F32.wireOp",EDGE,"E45"),sQuery(id+"F32.wireOp",EDGE,"E46"),sQuery(id+"F32.wireOp",EDGE,"E49"),sQuery(id+"F32.wireOp",EDGE,"E50"),sQuery(id+"F32.wireOp",EDGE,"E51")])],"isStart":false});
            var sketch = newSketch(context, id + "F60", { "sketchPlane" : qUnion([Q0])});
            skLineSegment(sketch, "E91", {"start": v(-4934.21, 9906) * mm, "end": v(-4934.21, 1270) * mm});
            skPoint(sketch, "E91.startSnap0", {"position": v(-4934.21, 3696.03) * mm});
            skPoint(sketch, "E92.firstSnap0", {"position": v(-4934.21, 5588) * mm});
            skLineSegment(sketch, "E92.bottom", {"start": v(-5490.93, 5588) * mm, "end": v(-4361.16, 5588) * mm});
            skLineSegment(sketch, "E92.top", {"start": v(-5490.93, 8636) * mm, "end": v(-4361.16, 8636) * mm});
            skLineSegment(sketch, "E92.left", {"start": v(-5490.93, 5588) * mm, "end": v(-5490.93, 8636) * mm});
            skLineSegment(sketch, "E92.right", {"start": v(-4361.16, 5588) * mm, "end": v(-4361.16, 8636) * mm});
            skSolve(sketch);
        }
        {
            var Q0;
            Q0 = qSketchRegion(id + "F60", true);
            extrude(context, id + "F61", {"entities" : qUnion([Q0]), "operationType" : NewBodyOperationType.ADD, "depth" : 889 * mm});
        }
        {
            var Q0;
            Q0=makeQuery(id+"F33.opExtrude","CAP_FACE",FACE,{"disambiguationData":[OSD([sQuery(id+"F32.wireOp",EDGE,"E42"),sQuery(id+"F32.wireOp",EDGE,"E43"),sQuery(id+"F32.wireOp",EDGE,"E44"),sQuery(id+"F32.wireOp",EDGE,"E45"),sQuery(id+"F32.wireOp",EDGE,"E46"),sQuery(id+"F32.wireOp",EDGE,"E49"),sQuery(id+"F32.wireOp",EDGE,"E50"),sQuery(id+"F32.wireOp",EDGE,"E51")])],"isStart":false});
            var sketch = newSketch(context, id + "F62", { "sketchPlane" : qUnion([Q0])});
            skLineSegment(sketch, "E93.bottom", {"start": v(-3665.36, 7994.32) * mm, "end": v(-3264.3, 7994.32) * mm});
            skLineSegment(sketch, "E93.top", {"start": v(-3665.36, 6370.05) * mm, "end": v(-3264.3, 6370.05) * mm});
            skLineSegment(sketch, "E93.left", {"start": v(-3665.36, 7994.32) * mm, "end": v(-3665.36, 6370.05) * mm});
            skLineSegment(sketch, "E93.right", {"start": v(-3264.3, 7994.32) * mm, "end": v(-3264.3, 6370.05) * mm});
            skSolve(sketch);
        }
        {
            var Q0;
            Q0 = qSketchRegion(id + "F62", true);
            extrude(context, id + "F63", {"entities" : qUnion([Q0]), "operationType" : NewBodyOperationType.ADD, "depth" : 889 * mm});
        }
        {
            var Q0;
            Q0=makeQuery(id+"F61.opExtrude","SWEPT_FACE",FACE,{"disambiguationData":[OSD([sQuery(id+"F60.wireOp",EDGE,"E92.left")])]});
            var sketch = newSketch(context, id + "F64", { "sketchPlane" : qUnion([Q0])});
            skCircle(sketch, "E94", {"center": v(16918.22, 7112) * mm, "radius": 2602.84 * mm});
            skPoint(sketch, "E94.centerSnap0", {"position": v(14808.2, 7112) * mm});
            skSolve(sketch);
        }
        {
            var Q0;
            Q0 = qSketchRegion(id + "F64", true);
            extrude(context, id + "F65", {"entities" : qUnion([Q0]), "operationType" : NewBodyOperationType.ADD, "oppositeDirection" : true, "depth" : 4495.8 * mm});
        }
        {
            var Q0;
            Q0=makeQuery(id+"F65.opExtrude","CAP_FACE",FACE,{"disambiguationData":[OSD([sQuery(id+"F64.wireOp",EDGE,"E94")])],"isStart":false});
            var sketch = newSketch(context, id + "F66", { "sketchPlane" : qUnion([Q0])});
            skLineSegment(sketch, "E95", {"start": v(-19521.06, 7112) * mm, "end": v(-16918.22, 7112) * mm});
            skLineSegment(sketch, "E96", {"start": v(-16918.22, 9714.84) * mm, "end": v(-16918.22, 4509.16) * mm});
            skPoint(sketch, "E96.startSnap0", {"position": v(-16918.22, 7112) * mm});
            skLineSegment(sketch, "E97", {"start": v(-18758.71, 8952.49) * mm, "end": v(-16918.22, 7112) * mm});
            skLineSegment(sketch, "E98", {"start": v(-18758.71, 5271.51) * mm, "end": v(-16918.22, 7112) * mm});
            skPoint(sketch, "E99.orphan", {"position": v(-14315.38, 7112) * mm});
            skCircle(sketch, "E100", {"center": v(-16918.22, 8636) * mm, "radius": 381 * mm});
            skCircle(sketch, "E101", {"center": v(-17995.86, 8189.63) * mm, "radius": 381 * mm});
            skCircle(sketch, "E102", {"center": v(-18442.22, 7112) * mm, "radius": 381 * mm});
            skCircle(sketch, "E103", {"center": v(-17995.86, 6034.37) * mm, "radius": 381 * mm});
            skCircle(sketch, "E104", {"center": v(-16918.22, 5588) * mm, "radius": 381 * mm});
            skCircle(sketch, "E105.MirrorC", {"center": v(-15840.6, 8189.63) * mm, "radius": 381 * mm});
            skCircle(sketch, "E106.MirrorC", {"center": v(-15394.22, 7112) * mm, "radius": 381 * mm});
            skCircle(sketch, "E107.MirrorC", {"center": v(-15840.6, 6034.37) * mm, "radius": 381 * mm});
            skSolve(sketch);
        }
        {
            var Q0;
            Q0 = qSketchRegion(id + "F66", true);
            extrude(context, id + "F67", {"entities" : qUnion([Q0]), "operationType" : NewBodyOperationType.ADD, "depth" : 2540 * mm});
        }
        {
            var Q0;
            Q0=makeQuery(id+"F65.opExtrude","CAP_FACE",FACE,{"disambiguationData":[OSD([sQuery(id+"F64.wireOp",EDGE,"E94")])],"isStart":false});
            cPlane(context, id + "F68", {"entities" : qUnion([Q0]), "cplaneType" : CPlaneType.OFFSET, "offset" : 762 * mm, "width" : 152.4 * mm, "height" : 152.4 * mm});
        }
        {
            var Q0;
            Q0=qCreatedBy(id+"F68.planeOp",FACE);
            var sketch = newSketch(context, id + "F69", { "sketchPlane" : qUnion([Q0])});
            skCircle(sketch, "E108", {"center": v(-16918.22, 7112) * mm, "radius": 2602.84 * mm});
            skSolve(sketch);
        }
        {
            var Q0;
            Q0 = qSketchRegion(id + "F69", true);
            extrude(context, id + "F70", {"entities" : qUnion([Q0]), "operationType" : NewBodyOperationType.ADD, "depth" : 508 * mm});
        }
        {
            var Q0;
            Q0=makeQuery(id+"F70.opExtrude","CAP_FACE",FACE,{"disambiguationData":[OSD([sQuery(id+"F69.wireOp",EDGE,"E108")])],"isStart":false});
            cPlane(context, id + "F71", {"entities" : qUnion([Q0]), "cplaneType" : CPlaneType.OFFSET, "offset" : 508 * mm, "width" : 152.4 * mm, "height" : 152.4 * mm});
        }
        {
            var Q0;
            Q0=qCreatedBy(id+"F71.planeOp",FACE);
            var sketch = newSketch(context, id + "F72", { "sketchPlane" : qUnion([Q0])});
            skCircle(sketch, "E109", {"center": v(-16918.22, 7112) * mm, "radius": 2602.84 * mm});
            skSolve(sketch);
        }
        {
            var Q0;
            Q0 = qSketchRegion(id + "F72", true);
            extrude(context, id + "F73", {"entities" : qUnion([Q0]), "operationType" : NewBodyOperationType.ADD, "depth" : 381 * mm});
        }
        {
            var Q0;
            Q0=makeQuery(id+"F73.opExtrude","CAP_FACE",FACE,{"disambiguationData":[OSD([sQuery(id+"F72.wireOp",EDGE,"E109")])],"isStart":false});
            var sketch = newSketch(context, id + "F74", { "sketchPlane" : qUnion([Q0])});
            skLineSegment(sketch, "E110.bottom", {"start": v(-18790.88, 9194.8) * mm, "end": v(-15056.23, 9194.8) * mm});
            skLineSegment(sketch, "E110.top", {"start": v(-18790.88, 10048.82) * mm, "end": v(-15056.23, 10048.82) * mm});
            skLineSegment(sketch, "E110.left", {"start": v(-18790.88, 9194.8) * mm, "end": v(-18790.88, 10048.82) * mm});
            skLineSegment(sketch, "E110.right", {"start": v(-15056.23, 9194.8) * mm, "end": v(-15056.23, 10048.82) * mm});
            skLineSegment(sketch, "E111.bottom", {"start": v(-19277.16, 5029.2) * mm, "end": v(-14972.37, 5029.2) * mm});
            skLineSegment(sketch, "E111.top", {"start": v(-19277.16, 4400.25) * mm, "end": v(-14972.37, 4400.25) * mm});
            skLineSegment(sketch, "E111.left", {"start": v(-19277.16, 5029.2) * mm, "end": v(-19277.16, 4400.25) * mm});
            skLineSegment(sketch, "E111.right", {"start": v(-14972.37, 5029.2) * mm, "end": v(-14972.37, 4400.25) * mm});
            skSolve(sketch);
        }
        {
            var Q0;
            Q0 = qSketchRegion(id + "F74", true);
            extrude(context, id + "F75", {"entities" : qUnion([Q0]), "operationType" : NewBodyOperationType.REMOVE, "endBound" : BoundingType.THROUGH_ALL, "oppositeDirection" : true, "depth" : 25.4 * mm});
        }
        {
            var Q0;
            Q0=makeQuery(id+"F75.boolean.opBoolean","COPY",FACE,{"disambiguationData":[TD([makeQuery(id+"F61.opExtrude","SWEPT_FACE",FACE,{"disambiguationData":[OSD([sQuery(id+"F60.wireOp",EDGE,"E92.left")])]})])],"derivedFrom":makeQuery(id+"F75.opExtrude","SWEPT_FACE",FACE,{"disambiguationData":[OSD([sQuery(id+"F74.wireOp",EDGE,"E110.bottom")])]})});
            var sketch = newSketch(context, id + "F76", { "sketchPlane" : qUnion([Q0])});
            skLineSegment(sketch, "E112.bottom", {"start": v(-1163.87, 16220.82) * mm, "end": v(5490.93, 16220.82) * mm});
            skLineSegment(sketch, "E112.top", {"start": v(-1163.87, 17615.62) * mm, "end": v(5490.93, 17615.62) * mm});
            skLineSegment(sketch, "E112.left", {"start": v(-1163.87, 16220.82) * mm, "end": v(-1163.87, 17615.62) * mm});
            skLineSegment(sketch, "E112.right", {"start": v(5490.93, 16220.82) * mm, "end": v(5490.93, 17615.62) * mm});
            skSolve(sketch);
        }
        {
            var Q0;
            Q0 = qSketchRegion(id + "F76", true);
            extrude(context, id + "F77", {"entities" : qUnion([Q0]), "operationType" : NewBodyOperationType.ADD, "depth" : 127 * mm});
        }
        {
            var Q0;
            Q0=makeQuery(id+"F77.opExtrude","CAP_EDGE",EDGE,{"disambiguationData":[OSD([sQuery(id+"F76.wireOp",EDGE,"E112.top")])],"isStart":false});
            var Q1;
            Q1=makeQuery(id+"F77.opExtrude","CAP_EDGE",EDGE,{"disambiguationData":[OSD([sQuery(id+"F76.wireOp",EDGE,"E112.bottom")])],"isStart":false});
            fillet(context, id + "F78", {"entities" : qUnion([Q0, Q1]), "radius" : 76.2 * mm, "tangentPropagation" : true, "allowEdgeOverflow" : false});
        }
        {
            var Q0;
            Q0=makeQuery(id+"F33.opExtrude","SWEPT_FACE",FACE,{"disambiguationData":[OSD([sQuery(id+"F32.wireOp",EDGE,"E44")])]});
            var sketch = newSketch(context, id + "F79", { "sketchPlane" : qUnion([Q0])});
            skLineSegment(sketch, "E113.bottom", {"start": v(1778, 4902.2) * mm, "end": v(9652, 4902.2) * mm});
            skLineSegment(sketch, "E113.top", {"start": v(1778, 13182.6) * mm, "end": v(9652, 13182.6) * mm});
            skLineSegment(sketch, "E113.left", {"start": v(1778, 4902.2) * mm, "end": v(1778, 13182.6) * mm});
            skLineSegment(sketch, "E113.right", {"start": v(9652, 4902.2) * mm, "end": v(9652, 13182.6) * mm});
            skSolve(sketch);
        }
        {
            var Q0;
            Q0 = qSketchRegion(id + "F79", true);
            extrude(context, id + "F80", {"entities" : qUnion([Q0]), "operationType" : NewBodyOperationType.ADD, "depth" : 1016 * mm});
        }
        {
            var Q0;
            Q0=makeQuery(id+"F80.opExtrude","SWEPT_FACE",FACE,{"disambiguationData":[OSD([sQuery(id+"F79.wireOp",EDGE,"E113.bottom")])]});
            var sketch = newSketch(context, id + "F81", { "sketchPlane" : qUnion([Q0])});
            skLineSegment(sketch, "E114", {"start": v(1778, 10922) * mm, "end": v(9652, 10414) * mm});
            skLineSegment(sketch, "E115", {"start": v(9652, 10414) * mm, "end": v(9889.85, 11538.8) * mm});
            skLineSegment(sketch, "E116", {"start": v(9889.85, 11538.8) * mm, "end": v(1778, 10922) * mm});
            skSolve(sketch);
        }
        {
            var Q0;
            Q0 = qSketchRegion(id + "F81", true);
            extrude(context, id + "F82", {"entities" : qUnion([Q0]), "operationType" : NewBodyOperationType.REMOVE, "endBound" : BoundingType.THROUGH_ALL, "oppositeDirection" : true, "depth" : 25.4 * mm});
        }
        {
            var Q0;
            {var subQ0=sQuery(id+"F32.wireOp",EDGE,"E44");Q0=makeQuery(id+"F80.boolean.opBoolean","SPLIT",FACE,{"disambiguationData":[TD([makeQuery(id+"F80.opExtrude","SWEPT_FACE",FACE,{"disambiguationData":[OSD([sQuery(id+"F79.wireOp",EDGE,"E113.bottom")])]})])],"derivedFrom":makeQuery(id+"F33.opExtrude","SWEPT_FACE",FACE,{"disambiguationData":[OSD([subQ0])]})});}
            cPlane(context, id + "F83", {"entities" : qUnion([Q0]), "cplaneType" : CPlaneType.OFFSET, "offset" : 1016 * mm, "width" : 152.4 * mm, "height" : 152.4 * mm});
        }
        {
            var Q0;
            Q0=qCreatedBy(id+"F83.planeOp",FACE);
            var sketch = newSketch(context, id + "F84", { "sketchPlane" : qUnion([Q0])});
            skLineSegment(sketch, "E117.bottom", {"start": v(1816.22, 10693.4) * mm, "end": v(6896.22, 10693.4) * mm});
            skLineSegment(sketch, "E117.top", {"start": v(1816.22, 7391.4) * mm, "end": v(6896.22, 7391.4) * mm});
            skLineSegment(sketch, "E117.left", {"start": v(1816.22, 10693.4) * mm, "end": v(1816.22, 7391.4) * mm});
            skLineSegment(sketch, "E117.right", {"start": v(6896.22, 10693.4) * mm, "end": v(6896.22, 7391.4) * mm});
            skSolve(sketch);
        }
        {
            var Q0;
            Q0 = qSketchRegion(id + "F84", true);
            extrude(context, id + "F85", {"entities" : qUnion([Q0]), "operationType" : NewBodyOperationType.ADD, "oppositeDirection" : true, "depth" : 1498.6 * mm});
        }
        {
            var Q0;
            Q0=makeQuery(id+"F80.opExtrude","SWEPT_FACE",FACE,{"disambiguationData":[OSD([sQuery(id+"F79.wireOp",EDGE,"E113.left")])]});
            var sketch = newSketch(context, id + "F86", { "sketchPlane" : qUnion([Q0])});
            skLineSegment(sketch, "E118", {"start": v(-7188.2, 10744.2) * mm, "end": v(-7373.1, 11252.2) * mm});
            skLineSegment(sketch, "E119", {"start": v(-7373.1, 11252.2) * mm, "end": v(-10779.32, 11252.2) * mm});
            skLineSegment(sketch, "E120", {"start": v(-10779.32, 11252.2) * mm, "end": v(-10896.6, 10744.2) * mm});
            skLineSegment(sketch, "E121", {"start": v(-10896.6, 10744.2) * mm, "end": v(-7188.2, 10744.2) * mm});
            skSolve(sketch);
        }
        {
            var Q0;
            Q0 = qSketchRegion(id + "F86", true);
            extrude(context, id + "F87", {"entities" : qUnion([Q0]), "operationType" : NewBodyOperationType.ADD, "oppositeDirection" : true, "depth" : 1320.8 * mm});
        }
        {
            var Q0;
            Q0=makeQuery(id+"F87.boolean.opBoolean","MERGE",FACE,{"derivedFrom":[makeQuery(id+"F80.opExtrude","SWEPT_FACE",FACE,{"disambiguationData":[OSD([sQuery(id+"F79.wireOp",EDGE,"E113.left")])]}),makeQuery(id+"F87.opExtrude","CAP_FACE",FACE,{"disambiguationData":[OSD([sQuery(id+"F86.wireOp",EDGE,"E118"),sQuery(id+"F86.wireOp",EDGE,"E119"),sQuery(id+"F86.wireOp",EDGE,"E120"),sQuery(id+"F86.wireOp",EDGE,"E121")])],"isStart":true})]});
            var sketch = newSketch(context, id + "F88", { "sketchPlane" : qUnion([Q0])});
            skLineSegment(sketch, "E122", {"start": v(-10678.3, 11125.2) * mm, "end": v(-7462.02, 11125.2) * mm});
            skLineSegment(sketch, "E123", {"start": v(-7462.02, 11125.2) * mm, "end": v(-7064.5, 10033) * mm});
            skLineSegment(sketch, "E124", {"start": v(-7064.5, 10033) * mm, "end": v(-10930.45, 10033) * mm});
            skLineSegment(sketch, "E125", {"start": v(-10930.45, 10033) * mm, "end": v(-10678.3, 11125.2) * mm});
            skSolve(sketch);
        }
        {
            var Q0;
            Q0 = qSketchRegion(id + "F88", true);
            extrude(context, id + "F89", {"entities" : qUnion([Q0]), "operationType" : NewBodyOperationType.REMOVE, "oppositeDirection" : true, "depth" : 127 * mm});
        }
        {
            var Q0;
            Q0=makeQuery(id+"F82.boolean.opBoolean","INTERSECT",EDGE,{"derivedFrom":[makeQuery(id+"F80.opExtrude","SWEPT_FACE",FACE,{"disambiguationData":[OSD([sQuery(id+"F79.wireOp",EDGE,"E113.top")])]}),makeQuery(id+"F82.opExtrude","SWEPT_FACE",FACE,{"disambiguationData":[OSD([sQuery(id+"F81.wireOp",EDGE,"E114")])]})]});
            var Q1;
            Q1=makeQuery(id+"F82.boolean.opBoolean","COPY",EDGE,{"derivedFrom":makeQuery(id+"F82.opExtrude","CAP_EDGE",EDGE,{"disambiguationData":[OSD([sQuery(id+"F81.wireOp",EDGE,"E114")])],"isStart":true})});
            chamfer(context, id + "F90", {"entities" : qUnion([Q0, Q1]), "width" : 254 * mm, "tangentPropagation" : true});
        }
    });
